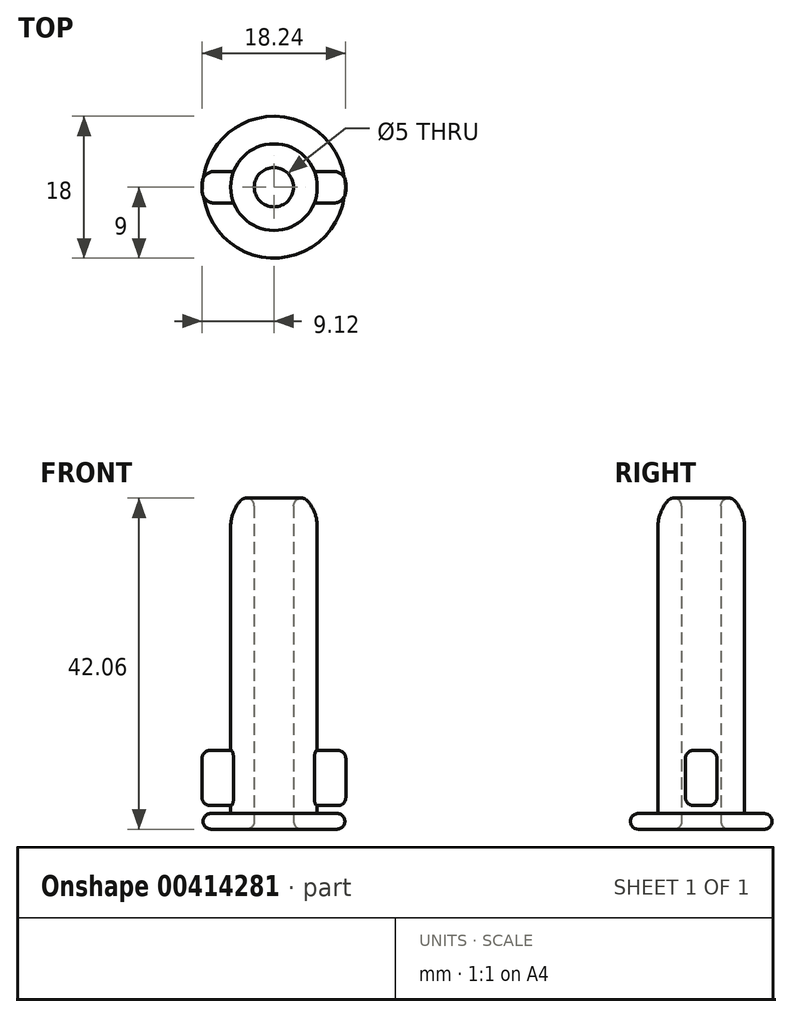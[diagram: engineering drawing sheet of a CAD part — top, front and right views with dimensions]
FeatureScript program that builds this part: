
annotation { "Feature Type Name" : "Feature", "Feature Type Description" : "" }
export const myFeature = defineFeature(function(context is Context, id is Id, definition is map)
    precondition{}
    {
        {
            var Q0;
            Q0=qCreatedBy(makeId("Top.planeOp"),FACE);
            var sketch = newSketch(context, id + "F0", { "sketchPlane" : qUnion([Q0])});
            skCircle(sketch, "E0", {"center": v(0, 0) * mm, "radius": 9 * mm});
            skCircle(sketch, "E1", {"center": v(0, 0) * mm, "radius": 2.5 * mm});
            skSolve(sketch);
        }
        {
            var Q0;
            Q0=makeQuery(id+"F0.imprint","IMPRINT",FACE,{"disambiguationData":[TD([[makeQuery(id+"F0.imprint","IMPRINT",EDGE,{"derivedFrom":sQuery(id+"F0.wireOp",EDGE,"E0")}),1.0]])]});
            extrude(context, id + "F1", {"entities" : qUnion([Q0]), "depth" : 2 * mm});
        }
        {
            var Q0;
            Q0=makeQuery(id+"F1.opExtrude","CAP_FACE",FACE,{"disambiguationData":[OSD([sQuery(id+"F0.wireOp",EDGE,"E0"),sQuery(id+"F0.wireOp",EDGE,"E1")])],"isStart":false});
            var sketch = newSketch(context, id + "F2", { "sketchPlane" : qUnion([Q0])});
            skCircle(sketch, "E2", {"center": v(0, 0) * mm, "radius": 5.5 * mm});
            skSolve(sketch);
        }
        {
            var Q0;
            Q0=makeQuery(id+"F2.imprint","IMPRINT",FACE,{"disambiguationData":[TD([[makeQuery(id+"F2.imprint","IMPRINT",EDGE,{"derivedFrom":sQuery(id+"F2.wireOp",EDGE,"E2")}),1.0]])]});
            extrude(context, id + "F3", {"entities" : qUnion([Q0]), "operationType" : NewBodyOperationType.ADD, "depth" : 1 * mm});
        }
        {
            var Q0;
            Q0=makeQuery(id+"F3.opExtrude","CAP_FACE",FACE,{"disambiguationData":[OSD([sQuery(id+"F0.wireOp",EDGE,"E1"),sQuery(id+"F2.wireOp",EDGE,"E2")])],"isStart":false});
            var sketch = newSketch(context, id + "F4", { "sketchPlane" : qUnion([Q0])});
            skCircle(sketch, "E3", {"center": v(0, 0) * mm, "radius": 5.5 * mm});
            skLineSegment(sketch, "E4.bottom", {"start": v(5.12, 2) * mm, "end": v(7.62, 2) * mm});
            skLineSegment(sketch, "E4.top", {"start": v(5.12, -2) * mm, "end": v(7.62, -2) * mm});
            skLineSegment(sketch, "E4.right", {"start": v(9.12, 0.5) * mm, "end": v(9.12, -0.5) * mm});
            skPoint(sketch, "E5.visualSharp", {"position": v(9.12, 2) * mm});
            skArc(sketch, "E5.filletArc", {"start": v(9.12, 0.5) * mm, "mid": v(8.68, 1.56) * mm, "end": v(7.62, 2) * mm});
            skPoint(sketch, "E6.visualSharp", {"position": v(9.12, -2) * mm});
            skArc(sketch, "E6.filletArc", {"start": v(7.62, -2) * mm, "mid": v(8.68, -1.56) * mm, "end": v(9.12, -0.5) * mm});
            skLineSegment(sketch, "E7.MirrorCS", {"start": v(-5.12, 2) * mm, "end": v(-7.62, 2) * mm});
            skArc(sketch, "E8.MirrorCS", {"start": v(-9.12, 0.5) * mm, "mid": v(-8.68, 1.56) * mm, "end": v(-7.62, 2) * mm});
            skArc(sketch, "E9.MirrorCS", {"start": v(-7.62, -2) * mm, "mid": v(-8.68, -1.56) * mm, "end": v(-9.12, -0.5) * mm});
            skLineSegment(sketch, "E10.MirrorCS", {"start": v(-5.12, -2) * mm, "end": v(-7.62, -2) * mm});
            skLineSegment(sketch, "E11", {"start": v(-9.12, -0.5) * mm, "end": v(-9.12, 0.5) * mm});
            skSolve(sketch);
        }
        {
            var Q0;
            Q0=makeQuery(id+"F4.imprint","IMPRINT",FACE,{"disambiguationData":[TD([[makeQuery(id+"F4.imprint","IMPRINT",EDGE,{"derivedFrom":makeQuery(id+"F3.opExtrude","CAP_EDGE",EDGE,{"disambiguationData":[OSD([sQuery(id+"F0.wireOp",EDGE,"E1")])],"isStart":false})}),-1.0]])]});
            extrude(context, id + "F5", {"entities" : qUnion([Q0]), "operationType" : NewBodyOperationType.ADD, "depth" : 40 * mm});
        }
        {
            var Q0;
            {var subQ0=sQuery(id+"F4.wireOp",EDGE,"E7.MirrorCS");Q0=makeQuery(id+"F4.imprint","IMPRINT",FACE,{"disambiguationData":[TD([[makeQuery(id+"F4.imprint","IMPRINT",EDGE,{"derivedFrom":subQ0}),1.0]])]});}
            var Q1;
            {var subQ1=sQuery(id+"F4.wireOp",EDGE,"E4.bottom");Q1=makeQuery(id+"F4.imprint","IMPRINT",FACE,{"disambiguationData":[TD([[makeQuery(id+"F4.imprint","IMPRINT",EDGE,{"derivedFrom":subQ1}),-1.0]])]});}
            extrude(context, id + "F6", {"entities" : qUnion([Q0, Q1]), "operationType" : NewBodyOperationType.ADD, "depth" : 7 * mm});
        }
        {
            var Q0;
            Q0=makeQuery(id+"F5.opExtrude","CAP_EDGE",EDGE,{"disambiguationData":[OSD([sQuery(id+"F4.wireOp",EDGE,"E3")])],"isStart":false});
            fillet(context, id + "F7", {"entities" : qUnion([Q0]), "radius" : 5 * mm, "tangentPropagation" : true, "allowEdgeOverflow" : false});
        }
        {
            var Q0;
            {var subQ0=sQuery(id+"F4.wireOp",EDGE,"E3");Q0=makeQuery(id+"F6.opExtrude","CAP_EDGE",EDGE,{"disambiguationData":[OSD([subQ0]),TDD([makeQuery(id+"F4.imprint","IMPRINT",EDGE,{"disambiguationData":[TD([[makeQuery(id+"F4.imprint","INTERSECT",VERTEX,{"derivedFrom":[subQ0,sQuery(id+"F4.wireOp",EDGE,"E4.bottom")]}),1.0]])],"derivedFrom":subQ0})])],"isStart":false});}
            var Q1;
            Q1=makeQuery(id+"F6.opExtrude","CAP_EDGE",EDGE,{"disambiguationData":[OSD([sQuery(id+"F4.wireOp",EDGE,"E5.filletArc"),sQuery(id+"F4.wireOp",EDGE,"E6.filletArc")])],"isStart":false});
            var Q2;
            {var subQ0=sQuery(id+"F4.wireOp",EDGE,"E3");Q2=makeQuery(id+"F6.opExtrude","CAP_EDGE",EDGE,{"disambiguationData":[OSD([subQ0]),TDD([makeQuery(id+"F4.imprint","IMPRINT",EDGE,{"disambiguationData":[TD([[makeQuery(id+"F4.imprint","INTERSECT",VERTEX,{"derivedFrom":[subQ0,sQuery(id+"F4.wireOp",EDGE,"E7.MirrorCS")]}),-1.0]])],"derivedFrom":subQ0})])],"isStart":false});}
            var Q3;
            Q3=makeQuery(id+"F6.opExtrude","CAP_EDGE",EDGE,{"disambiguationData":[OSD([sQuery(id+"F4.wireOp",EDGE,"E8.MirrorCS"),sQuery(id+"F4.wireOp",EDGE,"E9.MirrorCS")])],"isStart":false});
            var Q4;
            Q4=makeQuery(id+"F6.opExtrude","CAP_EDGE",EDGE,{"disambiguationData":[OSD([sQuery(id+"F4.wireOp",EDGE,"E8.MirrorCS"),sQuery(id+"F4.wireOp",EDGE,"E9.MirrorCS")])],"isStart":true});
            var Q5;
            Q5=makeQuery(id+"F6.opExtrude","CAP_EDGE",EDGE,{"disambiguationData":[OSD([sQuery(id+"F4.wireOp",EDGE,"E5.filletArc"),sQuery(id+"F4.wireOp",EDGE,"E6.filletArc")])],"isStart":true});
            var Q6;
            Q6=makeQuery(id+"F3.opExtrude","CAP_EDGE",EDGE,{"disambiguationData":[OSD([sQuery(id+"F2.wireOp",EDGE,"E2")])],"isStart":true});
            var Q7;
            Q7=makeQuery(id+"F1.opExtrude","CAP_EDGE",EDGE,{"disambiguationData":[OSD([sQuery(id+"F0.wireOp",EDGE,"E0")])],"isStart":false});
            var Q8;
            Q8=makeQuery(id+"F1.opExtrude","CAP_EDGE",EDGE,{"disambiguationData":[OSD([sQuery(id+"F0.wireOp",EDGE,"E0")])],"isStart":true});
            var Q9;
            Q9=makeQuery(id+"F1.opExtrude","CAP_EDGE",EDGE,{"disambiguationData":[OSD([sQuery(id+"F0.wireOp",EDGE,"E1")])],"isStart":true});
            var Q10;
            {var subQ0=sQuery(id+"F0.wireOp",EDGE,"E1");Q10=makeQuery(id+"F7.opFillet","BLEND_EDGE",EDGE,{"blendedFrom":[makeQuery(id+"F5.opExtrude","CAP_EDGE",EDGE,{"disambiguationData":[OSD([sQuery(id+"F4.wireOp",EDGE,"E3")])],"isStart":false}),makeQuery(id+"F5.boolean.opBoolean","MERGE",FACE,{"derivedFrom":[makeQuery(id+"F3.boolean.opBoolean","MERGE",FACE,{"derivedFrom":[makeQuery(id+"F1.opExtrude","SWEPT_FACE",FACE,{"disambiguationData":[OSD([subQ0])]}),makeQuery(id+"F3.opExtrude","SWEPT_FACE",FACE,{"disambiguationData":[OSD([subQ0])]})]}),makeQuery(id+"F5.opExtrude","SWEPT_FACE",FACE,{"disambiguationData":[OSD([subQ0])]})]})],"blendedInto":[makeQuery(id+"F5.boolean.opBoolean","MERGE",FACE,{"derivedFrom":[makeQuery(id+"F3.boolean.opBoolean","MERGE",FACE,{"derivedFrom":[makeQuery(id+"F1.opExtrude","SWEPT_FACE",FACE,{"disambiguationData":[OSD([subQ0])]}),makeQuery(id+"F3.opExtrude","SWEPT_FACE",FACE,{"disambiguationData":[OSD([subQ0])]})]}),makeQuery(id+"F5.opExtrude","SWEPT_FACE",FACE,{"disambiguationData":[OSD([subQ0])]})]})]});}
            fillet(context, id + "F8", {"entities" : qUnion([Q0, Q1, Q2, Q3, Q4, Q5, Q6, Q7, Q8, Q9, Q10]), "radius" : 1 * mm, "tangentPropagation" : true, "allowEdgeOverflow" : false});
        }
    });
